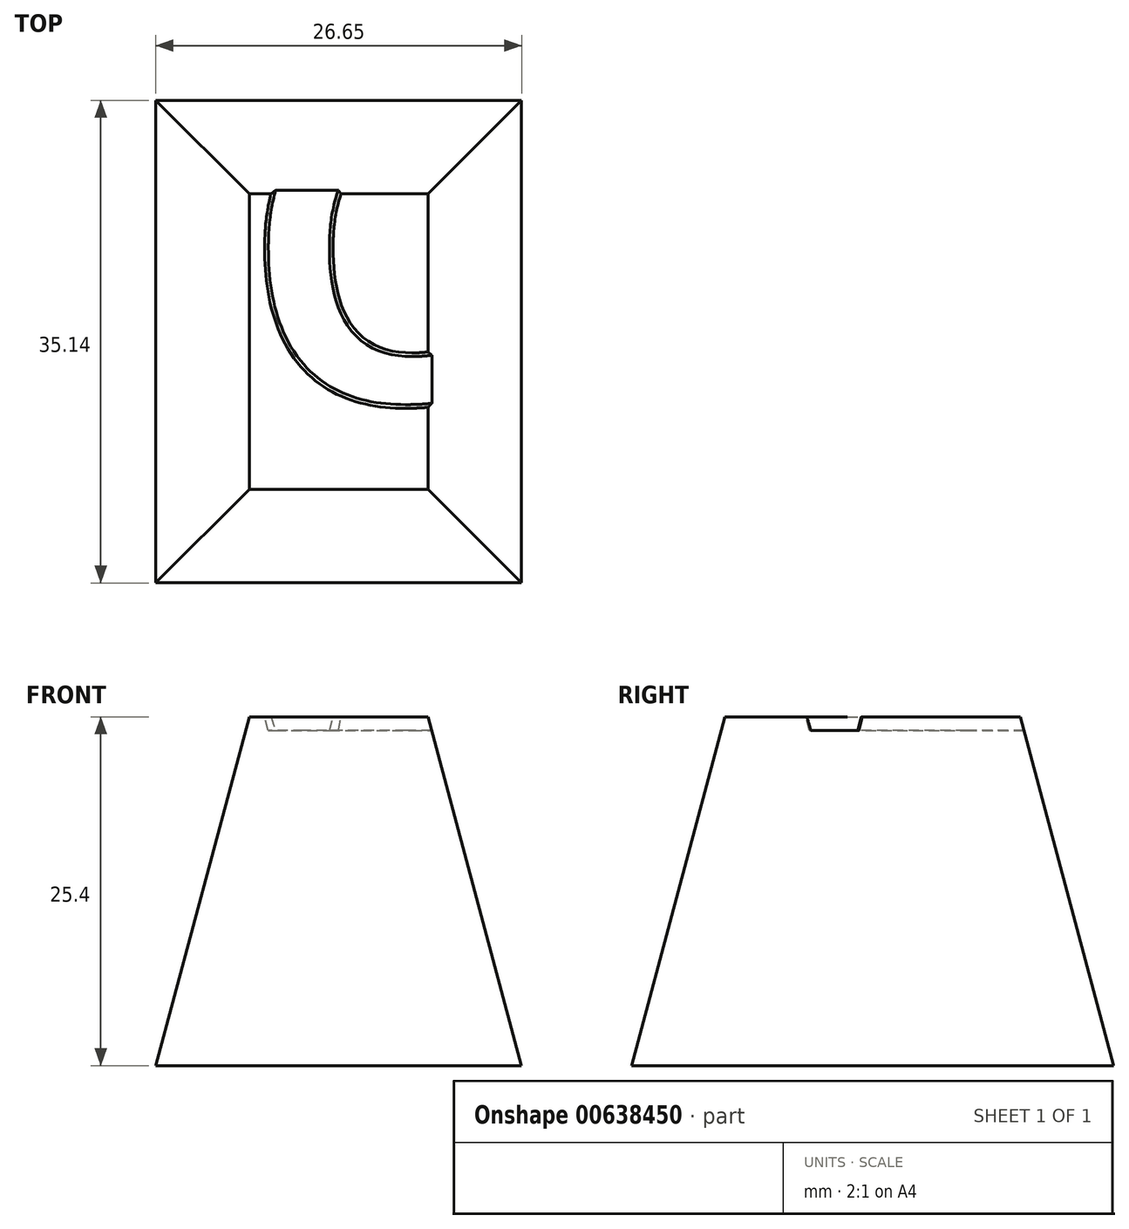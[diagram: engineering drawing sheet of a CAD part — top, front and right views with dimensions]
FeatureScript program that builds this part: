
annotation { "Feature Type Name" : "Feature", "Feature Type Description" : "" }
export const myFeature = defineFeature(function(context is Context, id is Id, definition is map)
    precondition{}
    {
        {
            var Q0;
            Q0=qCreatedBy(makeId("Top.planeOp"),FACE);
            var sketch = newSketch(context, id + "F0", { "sketchPlane" : qUnion([Q0])});
            skLineSegment(sketch, "E0.bottom", {"start": v(-49.75, 22.1) * mm, "end": v(-23.1, 22.1) * mm});
            skLineSegment(sketch, "E0.top", {"start": v(-49.75, -13.03) * mm, "end": v(-23.1, -13.03) * mm});
            skLineSegment(sketch, "E0.left", {"start": v(-49.75, 22.1) * mm, "end": v(-49.75, -13.03) * mm});
            skLineSegment(sketch, "E0.right", {"start": v(-23.1, 22.1) * mm, "end": v(-23.1, -13.03) * mm});
            skSolve(sketch);
        }
        {
            var Q0;
            Q0=makeQuery(id+"F0.imprint","IMPRINT",FACE,{"disambiguationData":[TD([[makeQuery(id+"F0.imprint","IMPRINT",EDGE,{"derivedFrom":sQuery(id+"F0.wireOp",EDGE,"E0.bottom")}),-1.0]])]});
            extrude(context, id + "F1", {"entities" : qUnion([Q0]), "depth" : 25.4 * mm, "offsetDistance" : 25.4 * mm, "hasDraft" : true, "draftAngle" : 15 * degree, "draftPullDirection" : true});
        }
        {
            var Q0;
            Q0=makeQuery(id+"F1.opExtrude","CAP_FACE",FACE,{"disambiguationData":[OSD([sQuery(id+"F0.wireOp",EDGE,"E0.bottom"),sQuery(id+"F0.wireOp",EDGE,"E0.top"),sQuery(id+"F0.wireOp",EDGE,"E0.left"),sQuery(id+"F0.wireOp",EDGE,"E0.right")])],"isStart":false});
            var sketch = newSketch(context, id + "F2", { "sketchPlane" : qUnion([Q0])});
            skText(sketch, "E1", { "text": "C", "fontName": "OpenSans-Bold.ttf"});
            const initialGuessF2  = {"E1": [-0.04368, 0, 1, 0, 0.02305]};
            skSetInitialGuess(sketch, initialGuessF2);
            skSolve(sketch);
        }
        {
            var Q0;
            Q0 = qSketchRegion(id + "F2", true);
            extrude(context, id + "F3", {"entities" : qUnion([Q0]), "operationType" : NewBodyOperationType.REMOVE, "oppositeDirection" : true, "depth" : 1 * mm, "offsetDistance" : 25 * mm, "hasDraft" : true, "draftAngle" : 15 * degree, "draftPullDirection" : true});
        }
    });
